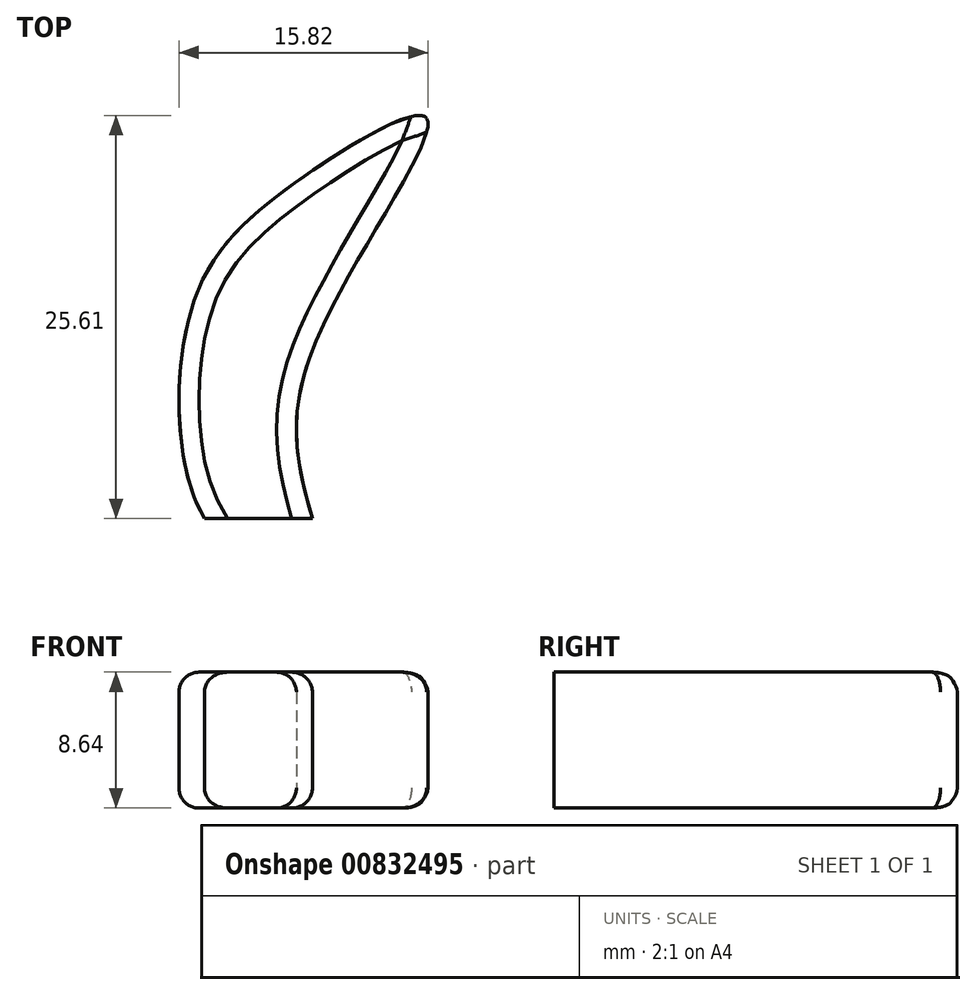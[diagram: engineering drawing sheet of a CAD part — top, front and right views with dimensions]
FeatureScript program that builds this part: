
annotation { "Feature Type Name" : "Feature", "Feature Type Description" : "" }
export const myFeature = defineFeature(function(context is Context, id is Id, definition is map)
    precondition{}
    {
        {
            var Q0;
            Q0=qCreatedBy(makeId("Top.planeOp"),FACE);
            var sketch = newSketch(context, id + "F0", { "sketchPlane" : qUnion([Q0])});
            skLineSegment(sketch, "E0", {"start": v(-14.12, 0) * mm, "end": v(-7.27, 0) * mm});
            skFitSpline(sketch, "E1", {"points": [v(-7.27, 0) * mm, v(-7.27, 10.69) * mm, v(0, 25.4) * mm, v(-8.38, 21.32) * mm, v(-15, 13.16) * mm, v(-14.12, 0) * mm], "startDerivative": vector(-14.88, 53.25) * mm, "endDerivative": vector(26.84, -44.75) * mm});
            skSolve(sketch);
        }
        {
            var Q0;
            Q0=makeQuery(id+"F0.imprint","IMPRINT",FACE,{"disambiguationData":[TD([[makeQuery(id+"F0.imprint","IMPRINT",EDGE,{"derivedFrom":sQuery(id+"F0.wireOp",EDGE,"E0")}),1.0]])]});
            extrude(context, id + "F1", {"entities" : qUnion([Q0]), "depth" : 8.64 * mm, "offsetDistance" : 25.4 * mm});
        }
        {
            var Q0;
            Q0=makeQuery(id+"F1.opExtrude","CAP_EDGE",EDGE,{"disambiguationData":[OSD([sQuery(id+"F0.wireOp",EDGE,"E1")])],"isStart":false});
            var Q1;
            Q1=makeQuery(id+"F1.opExtrude","CAP_EDGE",EDGE,{"disambiguationData":[OSD([sQuery(id+"F0.wireOp",EDGE,"E1")])],"isStart":true});
            fillet(context, id + "F2", {"entities" : qUnion([Q0, Q1]), "radius" : 1.27 * mm, "tangentPropagation" : true, "allowEdgeOverflow" : false});
        }
    });
